# Revit family: Pedestal-System_DHS-Adjustable-Pedestal_AWS
name_source: partatom
category: Generic Models
units: mm (PartAtom-declared; Revit-internal decimal feet)

## family parameters
Always vertical = Yes
Can host rebar = No
Cut with Voids When Loaded = No
Maintain Annotation Orientation = No
Part Type = Normal
Room Calculation Point = No
Round Connector Dimension = Use Diameter
Shared = No
Work Plane-Based = No

## types (9) — shared parameters
Default Elevation = 0' - 0"
Head Materials = Black
Keynote = 07 76 00
Manufacturer = Appian Way
Product Page URL = https://www.arcat.com
URL = https://paradigmwindows.com

## per-type parameters (varying)
| type | 1" | 1-1/2" | 1-1/4" | 1/2" | 1/4" | 1/8" | 3/4" |
| 1/8" | No | No | No | No | No | Yes | No |
| 1/4" | No | No | No | No | Yes | No | No |
| 1/2" | No | No | No | Yes | No | No | No |
| 3/4" | No | No | No | No | No | No | Yes |
| 1" | Yes | No | No | No | No | No | No |
| 1-1/4" | No | No | Yes | No | No | No | No |
| 1-1/2" | No | Yes | No | No | No | No | No |
| 1-3/8" to 2-1/4" | No | No | No | No | No | No | No |
| 2-3/8" to 30" (max.) | No | No | No | No | No | No | No |

type visibility flags (boolean, named after types; folded from table):
- 1/8": Yes: (none)
- 1/4": Yes: (none)
- 1/2": Yes: (none)
- 3/4": Yes: (none)
- 1": Yes: (none)
- 1-1/4": Yes: (none)
- 1-1/2": Yes: (none)
- 1-3/8" to 2-1/4": Yes: 1-3/8" to 2-1/4"
- 2-3/8" to 30" (max.): Yes: 2-3/8" to 30" (max.)

## geometry (parser evidence)
native form markers: Sweep x100
no freeform markers — native parametric forms only
